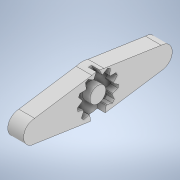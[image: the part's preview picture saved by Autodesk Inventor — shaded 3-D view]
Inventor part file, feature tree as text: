
AUTODESK INVENTOR PART (.ipt)
format: ipt  version: 2021 (Build 250183000, 183)  size: 188,928 bytes
history: native  units: mm
features: extrude x2, sketch x2
ambient origin geometry x8: Origin, YZ Plane, XZ Plane, XY Plane, X Axis, Y Axis, Z Axis, Center Point
bodies: Solid1 (feature_tree)
feature tree (4):
  extrude  "Extrusion1"  Depth=5.0mm TaperAngle=0.0deg
  extrude  "Extrusion2"  Depth=2.5mm TaperAngle=0.0deg
  sketch  "Sketch1"  dims[d0=7.0mm d1=20.0mm d2=5.0mm d3=0.0mm]
  sketch  "Sketch2"  dims[d5=110.0mm d8=0.5mm d9=20.071286mm d10=6.5mm d11=360.0deg d12=5.0mm d13=2.5mm d14=0.0mm d15=0.5mm d16=0.872665mm]
